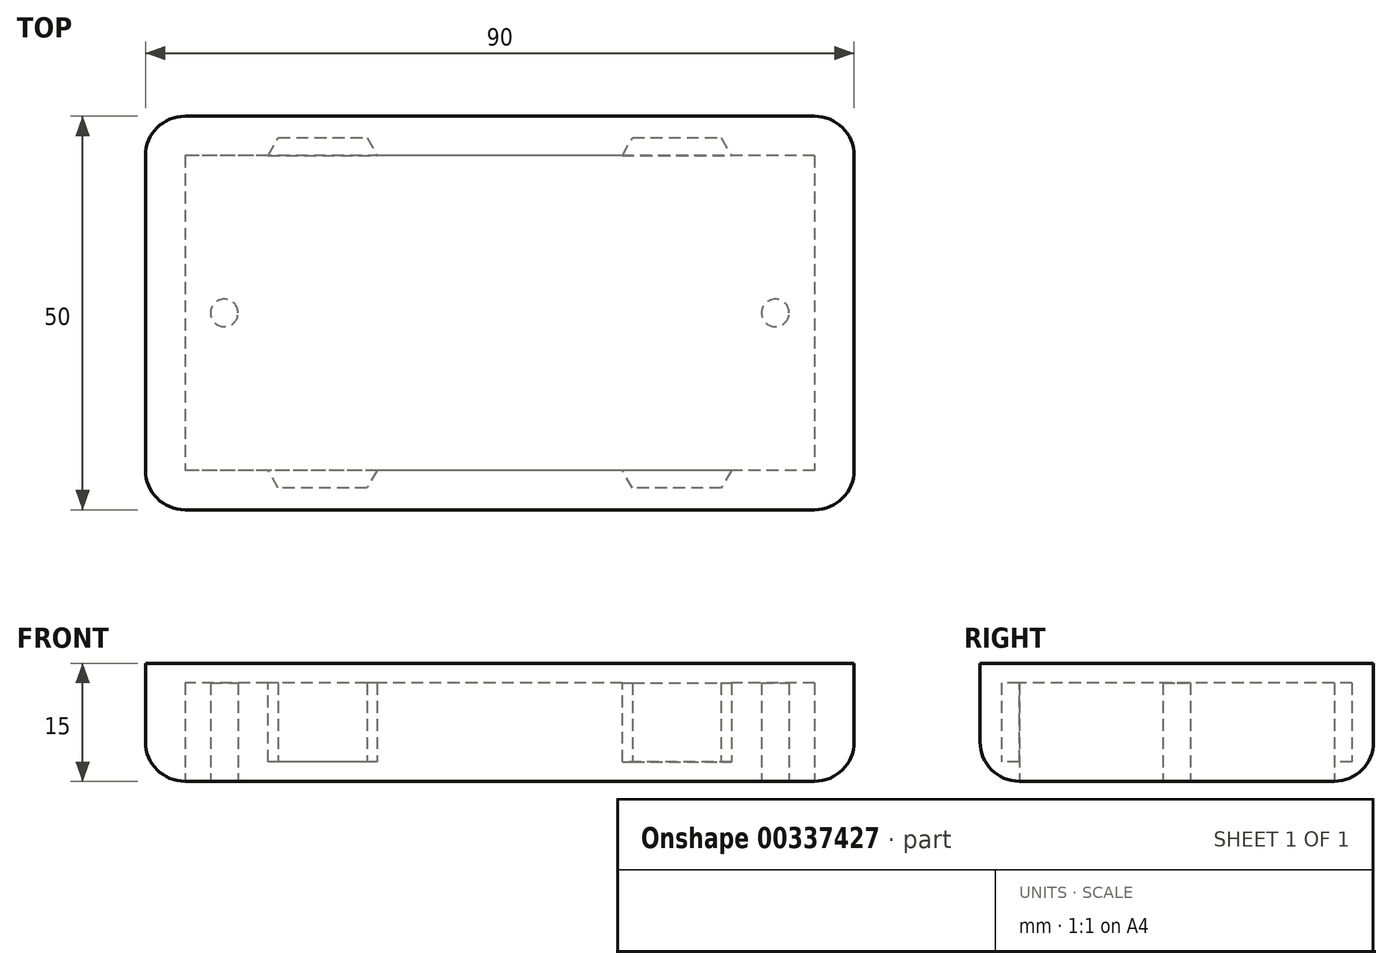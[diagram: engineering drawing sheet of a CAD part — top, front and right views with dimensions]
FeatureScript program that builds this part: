
annotation { "Feature Type Name" : "Feature", "Feature Type Description" : "" }
export const myFeature = defineFeature(function(context is Context, id is Id, definition is map)
    precondition{}
    {
        {
            var Q0;
            Q0=qCreatedBy(makeId("Top.planeOp"),FACE);
            var sketch = newSketch(context, id + "F0", { "sketchPlane" : qUnion([Q0])});
            skLineSegment(sketch, "E0.bottom", {"start": v(45, 25) * mm, "end": v(-45, 25) * mm});
            skLineSegment(sketch, "E0.top", {"start": v(45, -25) * mm, "end": v(-45, -25) * mm});
            skLineSegment(sketch, "E0.left", {"start": v(45, 25) * mm, "end": v(45, -25) * mm});
            skLineSegment(sketch, "E0.right", {"start": v(-45, 25) * mm, "end": v(-45, -25) * mm});
            skPoint(sketch, "E0.middle", {"position": v(0, 0) * mm});
            skLineSegment(sketch, "E1", {"start": v(45, 25) * mm, "end": v(0, 0) * mm, "construction": true});
            skLineSegment(sketch, "E2", {"start": v(0, 0) * mm, "end": v(45, 25) * mm, "construction": true});
            skLineSegment(sketch, "E3", {"start": v(0, 0) * mm, "end": v(-45, -25) * mm, "construction": true});
            skLineSegment(sketch, "E4", {"start": v(-45, 25) * mm, "end": v(0, 0) * mm, "construction": true});
            skLineSegment(sketch, "E5", {"start": v(0, 0) * mm, "end": v(45, -25) * mm, "construction": true});
            skPoint(sketch, "E6", {"position": v(22.5, 12.5) * mm});
            skPoint(sketch, "E7", {"position": v(22.5, -12.5) * mm});
            skPoint(sketch, "E8", {"position": v(-22.5, -12.5) * mm});
            skPoint(sketch, "E9", {"position": v(-22.5, 12.5) * mm});
            skCircle(sketch, "E10.cCircle", {"center": v(-22.5, 12.5) * mm, "radius": 9.75 * mm, "construction": true});
            skLineSegment(sketch, "E10.0", {"start": v(-16.87, 22.25) * mm, "end": v(-11.24, 12.5) * mm});
            skLineSegment(sketch, "E10.1", {"start": v(-11.24, 12.5) * mm, "end": v(-16.87, 2.75) * mm});
            skLineSegment(sketch, "E10.2", {"start": v(-16.87, 2.75) * mm, "end": v(-28.13, 2.75) * mm});
            skLineSegment(sketch, "E10.3", {"start": v(-28.13, 2.75) * mm, "end": v(-33.76, 12.5) * mm});
            skLineSegment(sketch, "E10.4", {"start": v(-33.76, 12.5) * mm, "end": v(-28.13, 22.25) * mm});
            skLineSegment(sketch, "E10.5", {"start": v(-28.13, 22.25) * mm, "end": v(-16.87, 22.25) * mm});
            skPoint(sketch, "E10.0.midPoint", {"position": v(-14.06, 17.37) * mm});
            skCircle(sketch, "E11.cCircle", {"center": v(22.5, 12.5) * mm, "radius": 9.75 * mm, "construction": true});
            skLineSegment(sketch, "E11.0", {"start": v(16.87, 22.25) * mm, "end": v(28.13, 22.25) * mm});
            skLineSegment(sketch, "E11.1", {"start": v(28.13, 22.25) * mm, "end": v(33.76, 12.5) * mm});
            skLineSegment(sketch, "E11.2", {"start": v(33.76, 12.5) * mm, "end": v(28.13, 2.75) * mm});
            skLineSegment(sketch, "E11.3", {"start": v(28.13, 2.75) * mm, "end": v(16.87, 2.75) * mm});
            skLineSegment(sketch, "E11.4", {"start": v(16.87, 2.75) * mm, "end": v(11.24, 12.5) * mm});
            skLineSegment(sketch, "E11.5", {"start": v(11.24, 12.5) * mm, "end": v(16.87, 22.25) * mm});
            skPoint(sketch, "E11.0.midPoint", {"position": v(22.5, 22.25) * mm});
            skCircle(sketch, "E12.cCircle", {"center": v(-22.5, -12.5) * mm, "radius": 9.75 * mm, "construction": true});
            skLineSegment(sketch, "E12.0", {"start": v(-16.87, -2.75) * mm, "end": v(-11.24, -12.5) * mm});
            skLineSegment(sketch, "E12.1", {"start": v(-11.24, -12.5) * mm, "end": v(-16.87, -22.25) * mm});
            skLineSegment(sketch, "E12.2", {"start": v(-16.87, -22.25) * mm, "end": v(-28.13, -22.25) * mm});
            skLineSegment(sketch, "E12.3", {"start": v(-28.13, -22.25) * mm, "end": v(-33.76, -12.5) * mm});
            skLineSegment(sketch, "E12.4", {"start": v(-33.76, -12.5) * mm, "end": v(-28.13, -2.75) * mm});
            skLineSegment(sketch, "E12.5", {"start": v(-28.13, -2.75) * mm, "end": v(-16.87, -2.75) * mm});
            skPoint(sketch, "E12.0.midPoint", {"position": v(-14.06, -7.63) * mm});
            skCircle(sketch, "E13.cCircle", {"center": v(22.5, -12.5) * mm, "radius": 9.75 * mm, "construction": true});
            skLineSegment(sketch, "E13.0", {"start": v(28.13, -2.75) * mm, "end": v(33.76, -12.5) * mm});
            skLineSegment(sketch, "E13.1", {"start": v(33.76, -12.5) * mm, "end": v(28.13, -22.25) * mm});
            skLineSegment(sketch, "E13.2", {"start": v(28.13, -22.25) * mm, "end": v(16.87, -22.25) * mm});
            skLineSegment(sketch, "E13.3", {"start": v(16.87, -22.25) * mm, "end": v(11.24, -12.5) * mm});
            skLineSegment(sketch, "E13.4", {"start": v(11.24, -12.5) * mm, "end": v(16.87, -2.75) * mm});
            skLineSegment(sketch, "E13.5", {"start": v(16.87, -2.75) * mm, "end": v(28.13, -2.75) * mm});
            skPoint(sketch, "E13.0.midPoint", {"position": v(30.94, -7.63) * mm});
            skSolve(sketch);
        }
        {
            var Q0;
            Q0=makeQuery(id+"F0.imprint","IMPRINT",FACE,{"disambiguationData":[TD([[makeQuery(id+"F0.imprint","IMPRINT",EDGE,{"derivedFrom":sQuery(id+"F0.wireOp",EDGE,"E0.bottom")}),1.0]])]});
            extrude(context, id + "F1", {"entities" : qUnion([Q0]), "depth" : 10 * mm});
        }
        {
            var Q0;
            Q0=makeQuery(id+"F1.opExtrude","CAP_FACE",FACE,{"disambiguationData":[OSD([sQuery(id+"F0.wireOp",EDGE,"E0.bottom"),sQuery(id+"F0.wireOp",EDGE,"E0.top"),sQuery(id+"F0.wireOp",EDGE,"E0.left"),sQuery(id+"F0.wireOp",EDGE,"E0.right"),sQuery(id+"F0.wireOp",EDGE,"E10.0"),sQuery(id+"F0.wireOp",EDGE,"E10.1"),sQuery(id+"F0.wireOp",EDGE,"E10.2"),sQuery(id+"F0.wireOp",EDGE,"E10.3"),sQuery(id+"F0.wireOp",EDGE,"E10.4"),sQuery(id+"F0.wireOp",EDGE,"E10.5"),sQuery(id+"F0.wireOp",EDGE,"E11.0"),sQuery(id+"F0.wireOp",EDGE,"E11.1"),sQuery(id+"F0.wireOp",EDGE,"E11.2"),sQuery(id+"F0.wireOp",EDGE,"E11.3"),sQuery(id+"F0.wireOp",EDGE,"E11.4"),sQuery(id+"F0.wireOp",EDGE,"E11.5"),sQuery(id+"F0.wireOp",EDGE,"E12.0"),sQuery(id+"F0.wireOp",EDGE,"E12.1"),sQuery(id+"F0.wireOp",EDGE,"E12.2"),sQuery(id+"F0.wireOp",EDGE,"E12.3"),sQuery(id+"F0.wireOp",EDGE,"E12.4"),sQuery(id+"F0.wireOp",EDGE,"E12.5"),sQuery(id+"F0.wireOp",EDGE,"E13.0"),sQuery(id+"F0.wireOp",EDGE,"E13.1"),sQuery(id+"F0.wireOp",EDGE,"E13.2"),sQuery(id+"F0.wireOp",EDGE,"E13.3"),sQuery(id+"F0.wireOp",EDGE,"E13.4"),sQuery(id+"F0.wireOp",EDGE,"E13.5")])],"isStart":false});
            var sketch = newSketch(context, id + "F2", { "sketchPlane" : qUnion([Q0])});
            skLineSegment(sketch, "E14.bottom", {"start": v(-45, 25) * mm, "end": v(45, 25) * mm});
            skLineSegment(sketch, "E14.top", {"start": v(-45, -25) * mm, "end": v(45, -25) * mm});
            skLineSegment(sketch, "E14.left", {"start": v(-45, 25) * mm, "end": v(-45, -25) * mm});
            skLineSegment(sketch, "E14.right", {"start": v(45, 25) * mm, "end": v(45, -25) * mm});
            skSolve(sketch);
        }
        {
            var Q0;
            Q0 = qSketchRegion(id + "F2", true);
            extrude(context, id + "F3", {"entities" : qUnion([Q0]), "operationType" : NewBodyOperationType.ADD, "depth" : 2.5 * mm});
        }
        {
            var Q0;
            Q0=makeQuery(id+"F1.opExtrude","CAP_FACE",FACE,{"disambiguationData":[OSD([sQuery(id+"F0.wireOp",EDGE,"E0.bottom"),sQuery(id+"F0.wireOp",EDGE,"E0.top"),sQuery(id+"F0.wireOp",EDGE,"E0.left"),sQuery(id+"F0.wireOp",EDGE,"E0.right"),sQuery(id+"F0.wireOp",EDGE,"E10.0"),sQuery(id+"F0.wireOp",EDGE,"E10.1"),sQuery(id+"F0.wireOp",EDGE,"E10.2"),sQuery(id+"F0.wireOp",EDGE,"E10.3"),sQuery(id+"F0.wireOp",EDGE,"E10.4"),sQuery(id+"F0.wireOp",EDGE,"E10.5"),sQuery(id+"F0.wireOp",EDGE,"E11.0"),sQuery(id+"F0.wireOp",EDGE,"E11.1"),sQuery(id+"F0.wireOp",EDGE,"E11.2"),sQuery(id+"F0.wireOp",EDGE,"E11.3"),sQuery(id+"F0.wireOp",EDGE,"E11.4"),sQuery(id+"F0.wireOp",EDGE,"E11.5"),sQuery(id+"F0.wireOp",EDGE,"E12.0"),sQuery(id+"F0.wireOp",EDGE,"E12.1"),sQuery(id+"F0.wireOp",EDGE,"E12.2"),sQuery(id+"F0.wireOp",EDGE,"E12.3"),sQuery(id+"F0.wireOp",EDGE,"E12.4"),sQuery(id+"F0.wireOp",EDGE,"E12.5"),sQuery(id+"F0.wireOp",EDGE,"E13.0"),sQuery(id+"F0.wireOp",EDGE,"E13.1"),sQuery(id+"F0.wireOp",EDGE,"E13.2"),sQuery(id+"F0.wireOp",EDGE,"E13.3"),sQuery(id+"F0.wireOp",EDGE,"E13.4"),sQuery(id+"F0.wireOp",EDGE,"E13.5")])],"isStart":true});
            var sketch = newSketch(context, id + "F4", { "sketchPlane" : qUnion([Q0])});
            skLineSegment(sketch, "E15.bottom", {"start": v(-45, 25) * mm, "end": v(45, 25) * mm});
            skLineSegment(sketch, "E15.top", {"start": v(-45, -25) * mm, "end": v(45, -25) * mm});
            skLineSegment(sketch, "E15.left", {"start": v(-45, 25) * mm, "end": v(-45, -25) * mm});
            skLineSegment(sketch, "E15.right", {"start": v(45, 25) * mm, "end": v(45, -25) * mm});
            skSolve(sketch);
        }
        {
            var Q0;
            Q0 = qSketchRegion(id + "F4", true);
            extrude(context, id + "F5", {"entities" : qUnion([Q0]), "operationType" : NewBodyOperationType.ADD, "depth" : 2.5 * mm});
        }
        {
            var Q0;
            Q0=makeQuery(id+"F5.boolean.opBoolean","MERGE",EDGE,{"derivedFrom":[makeQuery(id+"F3.boolean.opBoolean","MERGE",EDGE,{"derivedFrom":[makeQuery(id+"F1.opExtrude","SWEPT_EDGE",EDGE,{"disambiguationData":[OSD([sQuery(id+"F0.wireOp",EDGE,"E0.bottom"),sQuery(id+"F0.wireOp",EDGE,"E0.right")])]}),makeQuery(id+"F3.opExtrude","SWEPT_EDGE",EDGE,{"disambiguationData":[OSD([sQuery(id+"F2.wireOp",EDGE,"E14.bottom"),sQuery(id+"F2.wireOp",EDGE,"E14.left")])]})]}),makeQuery(id+"F5.opExtrude","SWEPT_EDGE",EDGE,{"disambiguationData":[OSD([sQuery(id+"F4.wireOp",EDGE,"E15.top"),sQuery(id+"F4.wireOp",EDGE,"E15.left")])]})]});
            var Q1;
            Q1=makeQuery(id+"F5.boolean.opBoolean","MERGE",EDGE,{"derivedFrom":[makeQuery(id+"F3.boolean.opBoolean","MERGE",EDGE,{"derivedFrom":[makeQuery(id+"F1.opExtrude","SWEPT_EDGE",EDGE,{"disambiguationData":[OSD([sQuery(id+"F0.wireOp",EDGE,"E0.bottom"),sQuery(id+"F0.wireOp",EDGE,"E0.left")])]}),makeQuery(id+"F3.opExtrude","SWEPT_EDGE",EDGE,{"disambiguationData":[OSD([sQuery(id+"F2.wireOp",EDGE,"E14.bottom"),sQuery(id+"F2.wireOp",EDGE,"E14.right")])]})]}),makeQuery(id+"F5.opExtrude","SWEPT_EDGE",EDGE,{"disambiguationData":[OSD([sQuery(id+"F4.wireOp",EDGE,"E15.top"),sQuery(id+"F4.wireOp",EDGE,"E15.right")])]})]});
            var Q2;
            Q2=makeQuery(id+"F5.boolean.opBoolean","MERGE",EDGE,{"derivedFrom":[makeQuery(id+"F3.boolean.opBoolean","MERGE",EDGE,{"derivedFrom":[makeQuery(id+"F1.opExtrude","SWEPT_EDGE",EDGE,{"disambiguationData":[OSD([sQuery(id+"F0.wireOp",EDGE,"E0.top"),sQuery(id+"F0.wireOp",EDGE,"E0.left")])]}),makeQuery(id+"F3.opExtrude","SWEPT_EDGE",EDGE,{"disambiguationData":[OSD([sQuery(id+"F2.wireOp",EDGE,"E14.top"),sQuery(id+"F2.wireOp",EDGE,"E14.right")])]})]}),makeQuery(id+"F5.opExtrude","SWEPT_EDGE",EDGE,{"disambiguationData":[OSD([sQuery(id+"F4.wireOp",EDGE,"E15.bottom"),sQuery(id+"F4.wireOp",EDGE,"E15.right")])]})]});
            var Q3;
            Q3=makeQuery(id+"F5.boolean.opBoolean","MERGE",EDGE,{"derivedFrom":[makeQuery(id+"F3.boolean.opBoolean","MERGE",EDGE,{"derivedFrom":[makeQuery(id+"F1.opExtrude","SWEPT_EDGE",EDGE,{"disambiguationData":[OSD([sQuery(id+"F0.wireOp",EDGE,"E0.top"),sQuery(id+"F0.wireOp",EDGE,"E0.right")])]}),makeQuery(id+"F3.opExtrude","SWEPT_EDGE",EDGE,{"disambiguationData":[OSD([sQuery(id+"F2.wireOp",EDGE,"E14.top"),sQuery(id+"F2.wireOp",EDGE,"E14.left")])]})]}),makeQuery(id+"F5.opExtrude","SWEPT_EDGE",EDGE,{"disambiguationData":[OSD([sQuery(id+"F4.wireOp",EDGE,"E15.bottom"),sQuery(id+"F4.wireOp",EDGE,"E15.left")])]})]});
            fillet(context, id + "F6", {"entities" : qUnion([Q0, Q1, Q2, Q3]), "radius" : 5 * mm, "tangentPropagation" : true, "allowEdgeOverflow" : false});
        }
        {
            var Q0;
            Q0=makeQuery(id+"F5.opExtrude","CAP_EDGE",EDGE,{"disambiguationData":[OSD([sQuery(id+"F4.wireOp",EDGE,"E15.bottom")])],"isStart":false});
            var Q1;
            {var subQ0=sQuery(id+"F4.wireOp",EDGE,"E15.right");var subQ1=sQuery(id+"F4.wireOp",EDGE,"E15.bottom");Q1=makeQuery(id+"F6.opFillet","BLEND_EDGE",EDGE,{"blendedFrom":[makeQuery(id+"F5.boolean.opBoolean","MERGE",EDGE,{"derivedFrom":[makeQuery(id+"F3.boolean.opBoolean","MERGE",EDGE,{"derivedFrom":[makeQuery(id+"F1.opExtrude","SWEPT_EDGE",EDGE,{"disambiguationData":[OSD([sQuery(id+"F0.wireOp",EDGE,"E0.top"),sQuery(id+"F0.wireOp",EDGE,"E0.left")])]}),makeQuery(id+"F3.opExtrude","SWEPT_EDGE",EDGE,{"disambiguationData":[OSD([sQuery(id+"F2.wireOp",EDGE,"E14.top"),sQuery(id+"F2.wireOp",EDGE,"E14.right")])]})]}),makeQuery(id+"F5.opExtrude","SWEPT_EDGE",EDGE,{"disambiguationData":[OSD([subQ1,subQ0])]})]}),makeQuery(id+"F5.opExtrude","CAP_FACE",FACE,{"disambiguationData":[OSD([subQ1,sQuery(id+"F4.wireOp",EDGE,"E15.top"),sQuery(id+"F4.wireOp",EDGE,"E15.left"),subQ0])],"isStart":false})],"blendedInto":[makeQuery(id+"F5.opExtrude","CAP_FACE",FACE,{"disambiguationData":[OSD([subQ1,sQuery(id+"F4.wireOp",EDGE,"E15.top"),sQuery(id+"F4.wireOp",EDGE,"E15.left"),subQ0])],"isStart":false})]});}
            var Q2;
            Q2=makeQuery(id+"F5.opExtrude","CAP_EDGE",EDGE,{"disambiguationData":[OSD([sQuery(id+"F4.wireOp",EDGE,"E15.right")])],"isStart":false});
            var Q3;
            {var subQ0=sQuery(id+"F4.wireOp",EDGE,"E15.right");var subQ1=sQuery(id+"F4.wireOp",EDGE,"E15.top");Q3=makeQuery(id+"F6.opFillet","BLEND_EDGE",EDGE,{"blendedFrom":[makeQuery(id+"F5.boolean.opBoolean","MERGE",EDGE,{"derivedFrom":[makeQuery(id+"F3.boolean.opBoolean","MERGE",EDGE,{"derivedFrom":[makeQuery(id+"F1.opExtrude","SWEPT_EDGE",EDGE,{"disambiguationData":[OSD([sQuery(id+"F0.wireOp",EDGE,"E0.bottom"),sQuery(id+"F0.wireOp",EDGE,"E0.left")])]}),makeQuery(id+"F3.opExtrude","SWEPT_EDGE",EDGE,{"disambiguationData":[OSD([sQuery(id+"F2.wireOp",EDGE,"E14.bottom"),sQuery(id+"F2.wireOp",EDGE,"E14.right")])]})]}),makeQuery(id+"F5.opExtrude","SWEPT_EDGE",EDGE,{"disambiguationData":[OSD([subQ1,subQ0])]})]}),makeQuery(id+"F5.opExtrude","CAP_FACE",FACE,{"disambiguationData":[OSD([sQuery(id+"F4.wireOp",EDGE,"E15.bottom"),subQ1,sQuery(id+"F4.wireOp",EDGE,"E15.left"),subQ0])],"isStart":false})],"blendedInto":[makeQuery(id+"F5.opExtrude","CAP_FACE",FACE,{"disambiguationData":[OSD([sQuery(id+"F4.wireOp",EDGE,"E15.bottom"),subQ1,sQuery(id+"F4.wireOp",EDGE,"E15.left"),subQ0])],"isStart":false})]});}
            var Q4;
            Q4=makeQuery(id+"F5.opExtrude","CAP_EDGE",EDGE,{"disambiguationData":[OSD([sQuery(id+"F4.wireOp",EDGE,"E15.top")])],"isStart":false});
            var Q5;
            Q5=makeQuery(id+"F5.opExtrude","CAP_EDGE",EDGE,{"disambiguationData":[OSD([sQuery(id+"F4.wireOp",EDGE,"E15.left")])],"isStart":false});
            var Q6;
            {var subQ0=sQuery(id+"F4.wireOp",EDGE,"E15.left");var subQ1=sQuery(id+"F4.wireOp",EDGE,"E15.top");Q6=makeQuery(id+"F6.opFillet","BLEND_EDGE",EDGE,{"blendedFrom":[makeQuery(id+"F5.boolean.opBoolean","MERGE",EDGE,{"derivedFrom":[makeQuery(id+"F3.boolean.opBoolean","MERGE",EDGE,{"derivedFrom":[makeQuery(id+"F1.opExtrude","SWEPT_EDGE",EDGE,{"disambiguationData":[OSD([sQuery(id+"F0.wireOp",EDGE,"E0.bottom"),sQuery(id+"F0.wireOp",EDGE,"E0.right")])]}),makeQuery(id+"F3.opExtrude","SWEPT_EDGE",EDGE,{"disambiguationData":[OSD([sQuery(id+"F2.wireOp",EDGE,"E14.bottom"),sQuery(id+"F2.wireOp",EDGE,"E14.left")])]})]}),makeQuery(id+"F5.opExtrude","SWEPT_EDGE",EDGE,{"disambiguationData":[OSD([subQ1,subQ0])]})]}),makeQuery(id+"F5.opExtrude","CAP_FACE",FACE,{"disambiguationData":[OSD([sQuery(id+"F4.wireOp",EDGE,"E15.bottom"),subQ1,subQ0,sQuery(id+"F4.wireOp",EDGE,"E15.right")])],"isStart":false})],"blendedInto":[makeQuery(id+"F5.opExtrude","CAP_FACE",FACE,{"disambiguationData":[OSD([sQuery(id+"F4.wireOp",EDGE,"E15.bottom"),subQ1,subQ0,sQuery(id+"F4.wireOp",EDGE,"E15.right")])],"isStart":false})]});}
            var Q7;
            {var subQ0=sQuery(id+"F4.wireOp",EDGE,"E15.left");var subQ1=sQuery(id+"F4.wireOp",EDGE,"E15.bottom");Q7=makeQuery(id+"F6.opFillet","BLEND_EDGE",EDGE,{"blendedFrom":[makeQuery(id+"F5.boolean.opBoolean","MERGE",EDGE,{"derivedFrom":[makeQuery(id+"F3.boolean.opBoolean","MERGE",EDGE,{"derivedFrom":[makeQuery(id+"F1.opExtrude","SWEPT_EDGE",EDGE,{"disambiguationData":[OSD([sQuery(id+"F0.wireOp",EDGE,"E0.top"),sQuery(id+"F0.wireOp",EDGE,"E0.right")])]}),makeQuery(id+"F3.opExtrude","SWEPT_EDGE",EDGE,{"disambiguationData":[OSD([sQuery(id+"F2.wireOp",EDGE,"E14.top"),sQuery(id+"F2.wireOp",EDGE,"E14.left")])]})]}),makeQuery(id+"F5.opExtrude","SWEPT_EDGE",EDGE,{"disambiguationData":[OSD([subQ1,subQ0])]})]}),makeQuery(id+"F5.opExtrude","CAP_FACE",FACE,{"disambiguationData":[OSD([subQ1,sQuery(id+"F4.wireOp",EDGE,"E15.top"),subQ0,sQuery(id+"F4.wireOp",EDGE,"E15.right")])],"isStart":false})],"blendedInto":[makeQuery(id+"F5.opExtrude","CAP_FACE",FACE,{"disambiguationData":[OSD([subQ1,sQuery(id+"F4.wireOp",EDGE,"E15.top"),subQ0,sQuery(id+"F4.wireOp",EDGE,"E15.right")])],"isStart":false})]});}
            fillet(context, id + "F7", {"entities" : qUnion([Q0, Q1, Q2, Q3, Q4, Q5, Q6, Q7]), "radius" : 5 * mm, "tangentPropagation" : true, "allowEdgeOverflow" : false});
        }
        {
            var Q0;
            Q0=makeQuery(id+"F5.opExtrude","CAP_FACE",FACE,{"disambiguationData":[OSD([sQuery(id+"F4.wireOp",EDGE,"E15.bottom"),sQuery(id+"F4.wireOp",EDGE,"E15.top"),sQuery(id+"F4.wireOp",EDGE,"E15.left"),sQuery(id+"F4.wireOp",EDGE,"E15.right")])],"isStart":false});
            var sketch = newSketch(context, id + "F8", { "sketchPlane" : qUnion([Q0])});
            skLineSegment(sketch, "E16", {"start": v(-40, 0) * mm, "end": v(40, 0) * mm});
            skLineSegment(sketch, "E17", {"start": v(40, 0) * mm, "end": v(35, 0) * mm});
            skLineSegment(sketch, "E18", {"start": v(-40, 0) * mm, "end": v(-35, 0) * mm});
            skCircle(sketch, "E19", {"center": v(-35, 0) * mm, "radius": 1.75 * mm});
            skCircle(sketch, "E20", {"center": v(35, 0) * mm, "radius": 1.75 * mm});
            skSolve(sketch);
        }
        {
            var Q0;
            {var subQ0=sQuery(id+"F8.wireOp",EDGE,"E18");var subQ1=sQuery(id+"F8.wireOp",EDGE,"E16");var subQ2=makeQuery(id+"F8.imprint","INTERSECT",VERTEX,{"derivedFrom":[subQ1,subQ0]});Q0=makeQuery(id+"F8.imprint","IMPRINT",FACE,{"disambiguationData":[TD([[makeQuery(id+"F8.imprint","IMPRINT",EDGE,{"disambiguationData":[TD([[subQ2,-1.0]])],"derivedFrom":subQ1}),-1.0]])]});}
            var Q1;
            {var subQ0=sQuery(id+"F8.wireOp",EDGE,"E18");var subQ1=sQuery(id+"F8.wireOp",EDGE,"E16");var subQ2=makeQuery(id+"F8.imprint","INTERSECT",VERTEX,{"derivedFrom":[subQ1,subQ0]});Q1=makeQuery(id+"F8.imprint","IMPRINT",FACE,{"disambiguationData":[TD([[makeQuery(id+"F8.imprint","IMPRINT",EDGE,{"disambiguationData":[TD([[subQ2,-1.0]])],"derivedFrom":subQ1}),1.0]])]});}
            var Q2;
            {var subQ0=sQuery(id+"F8.wireOp",EDGE,"E17");var subQ1=sQuery(id+"F8.wireOp",EDGE,"E16");var subQ2=makeQuery(id+"F8.imprint","INTERSECT",VERTEX,{"derivedFrom":[subQ1,subQ0]});Q2=makeQuery(id+"F8.imprint","IMPRINT",FACE,{"disambiguationData":[TD([[makeQuery(id+"F8.imprint","IMPRINT",EDGE,{"disambiguationData":[TD([[subQ2,1.0]])],"derivedFrom":subQ1}),-1.0]])]});}
            var Q3;
            {var subQ0=sQuery(id+"F8.wireOp",EDGE,"E17");var subQ1=sQuery(id+"F8.wireOp",EDGE,"E16");var subQ2=makeQuery(id+"F8.imprint","INTERSECT",VERTEX,{"derivedFrom":[subQ1,subQ0]});Q3=makeQuery(id+"F8.imprint","IMPRINT",FACE,{"disambiguationData":[TD([[makeQuery(id+"F8.imprint","IMPRINT",EDGE,{"disambiguationData":[TD([[subQ2,1.0]])],"derivedFrom":subQ1}),1.0]])]});}
            extrude(context, id + "F9", {"entities" : qUnion([Q0, Q1, Q2, Q3]), "operationType" : NewBodyOperationType.REMOVE, "oppositeDirection" : true, "depth" : 12.5 * mm});
        }
    });
